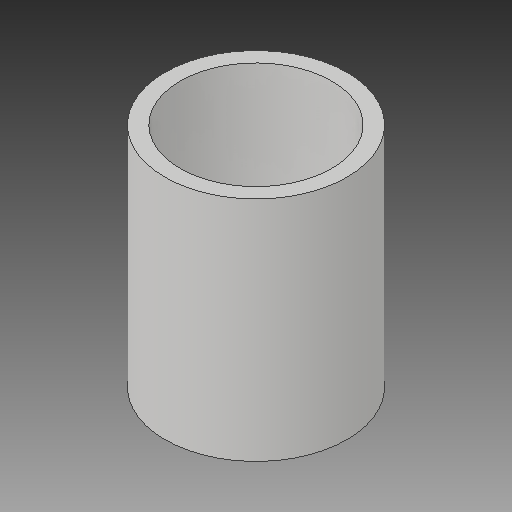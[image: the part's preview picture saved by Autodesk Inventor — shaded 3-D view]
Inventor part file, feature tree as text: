
AUTODESK INVENTOR PART (.ipt)
format: ipt  version: 2017 (Build 210142000, 142)  size: 98,304 bytes
history: native  units: mm
features: other x1, extrude x1, sketch x1
ambient origin geometry x8: Origin, YZ Plane, XZ Plane, XY Plane, X Axis, Y Axis, Z Axis, Center Point
bodies: Body1 (feature_tree)
feature tree (3):
  other  "Sólido1"
  extrude  "Extrusión1"  Depth=15.0mm
  sketch  "Boceto1"  dims[d0=10.0mm d1=1.0mm d2=15.0mm d3=0.0mm]
